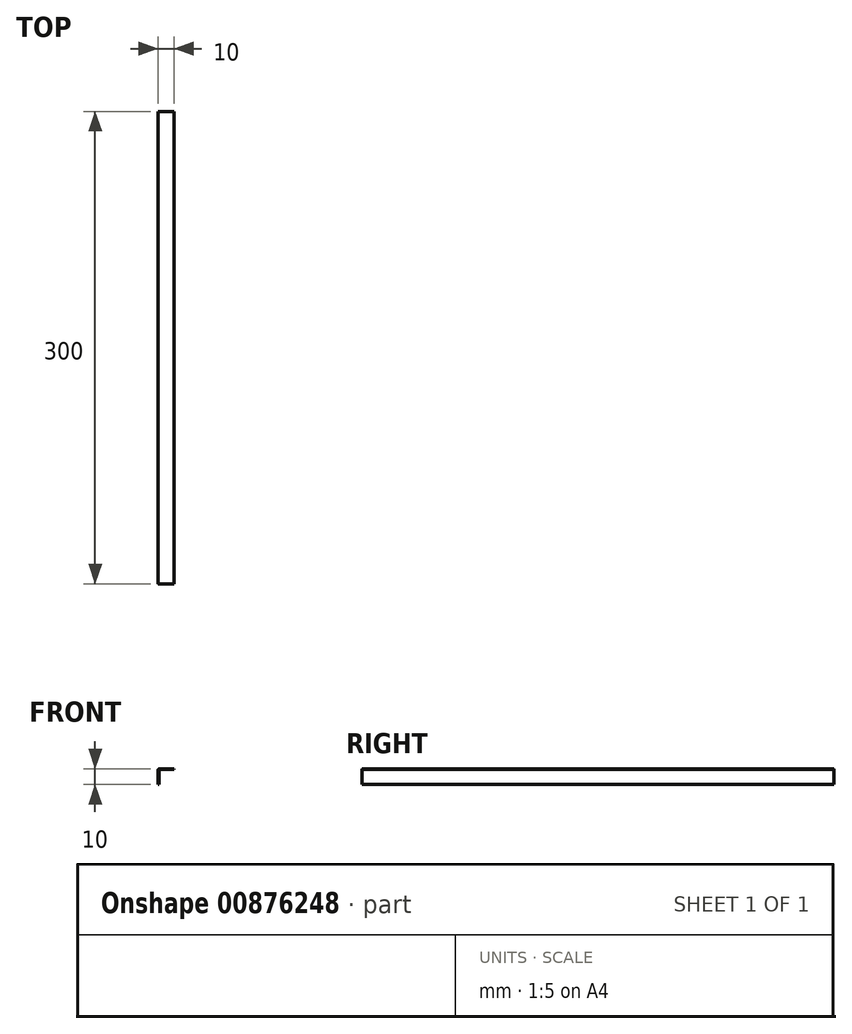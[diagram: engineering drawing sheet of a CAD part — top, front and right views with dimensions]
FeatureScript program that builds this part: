
annotation { "Feature Type Name" : "Feature", "Feature Type Description" : "" }
export const myFeature = defineFeature(function(context is Context, id is Id, definition is map)
    precondition{}
    {
        {
            var Q0;
            Q0=qCreatedBy(makeId("Front.planeOp"),FACE);
            var sketch = newSketch(context, id + "F0", { "sketchPlane" : qUnion([Q0])});
            skLineSegment(sketch, "E0", {"start": v(0, 0) * mm, "end": v(0, 9.25) * mm});
            skLineSegment(sketch, "E1", {"start": v(0.75, 10) * mm, "end": v(10, 10) * mm});
            skLineSegment(sketch, "E2", {"start": v(10, 10) * mm, "end": v(10, 9.5) * mm});
            skLineSegment(sketch, "E3", {"start": v(10, 9.5) * mm, "end": v(1, 9.5) * mm});
            skLineSegment(sketch, "E4", {"start": v(0.5, 9) * mm, "end": v(0.5, 0) * mm});
            skLineSegment(sketch, "E5", {"start": v(0, 0) * mm, "end": v(0.5, 0) * mm});
            skPoint(sketch, "E6.visualSharp", {"position": v(0.5, 9.5) * mm});
            skArc(sketch, "E6.filletArc", {"start": v(1, 9.5) * mm, "mid": v(0.65, 9.35) * mm, "end": v(0.5, 9) * mm});
            skPoint(sketch, "E7.visualSharp", {"position": v(0, 10) * mm});
            skArc(sketch, "E7.filletArc", {"start": v(0.75, 10) * mm, "mid": v(0.22, 9.78) * mm, "end": v(0, 9.25) * mm});
            skSolve(sketch);
        }
        {
            var Q0;
            Q0=makeQuery(id+"F0.imprint","IMPRINT",FACE,{"disambiguationData":[TD([[makeQuery(id+"F0.imprint","IMPRINT",EDGE,{"derivedFrom":sQuery(id+"F0.wireOp",EDGE,"E0")}),-1.0]])]});
            extrude(context, id + "F1", {"entities" : qUnion([Q0]), "depth" : 300 * mm, "offsetDistance" : 25.4 * mm});
        }
    });
